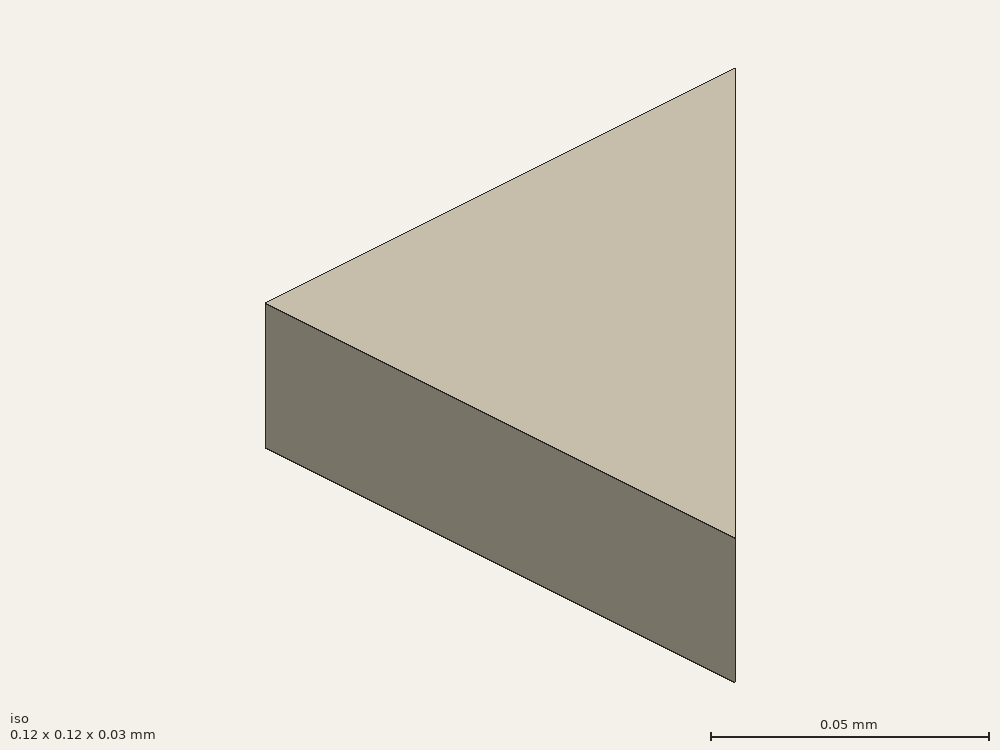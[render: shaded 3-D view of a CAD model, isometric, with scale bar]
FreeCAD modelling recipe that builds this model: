
FCSTD DOCUMENT  (FreeCAD 0.15R4671 (Git))
Label: triangle1
License: All rights reserved
LicenseURL: http://en.wikipedia.org/wiki/All_rights_reserved
objects: Sketcher::SketchObject×1, PartDesign::Pad×1
note: 3 computed .brp shape members not serialized (recipe doc carries the construction recipe); baked Part::Feature solids carry a one-line shape summary decoded from their .brp

FEATURE [Sketcher::SketchObject] Sketch
  sketch-geometry (3):
    g0: LineSegment StartX=-0.04 StartY=0.04 StartZ=0 EndX=-0.04 EndY=-0.08 EndZ=0
    g1: LineSegment StartX=-0.04 StartY=-0.08 StartZ=0 EndX=0.08 EndY=0.04 EndZ=0
    g2: LineSegment StartX=0.08 StartY=0.04 StartZ=0 EndX=-0.04 EndY=0.04 EndZ=0
  constraints (9):
    c: Coincident(g0,g1)
    c: Coincident(g1,g2)
    c: Coincident(g0,g2)
    c: Vertical(g0)
    c: DistanceY(g0) = -0.12
    c: Distance(g1,g0) = 0.12
    c: Perpendicular(g0,g2)
    c: Distance(g-1,g2) = 0.04
    c: Distance(g-1,g0) = 0.04
FEATURE [PartDesign::Pad] Pad
  Length = 0.03
  Length2 = 100
  Midplane = true
  Sketch = -> Sketch
  Type = 0
